# Revit family: 511_CA_HR-A_nailfin
name_source: partatom
category: Windows
revit_build: Autodesk Revit 2016 (Build: 20150220_1215(x64)
units: mm (PartAtom-declared; Revit-internal decimal feet)

## family parameters
Always vertical = Yes
Cut with Voids When Loaded = No
Host = Wall
OmniClass Number = 23.30.20.00
OmniClass Title = Windows
Room Calculation Point = No
Shared = No

## types (35) — shared parameters
Default Sill Height = 31 1/2"
MLW1 = 3 1/4"
MLW2 = 3 5/8"
MLW3 = 2 13/16"
Rough Height = 4 1/2"
Rough Width = 4 1/2"
Wall Closure = By host

## per-type parameters (varying)
| type | Bar Set | Height | MDLW | MLH | MLW4 | Width |
| 24x48 | 36" | 48" | 18" | 18" | 3" | 24" |
| 36x60 | 42" | 60" | 20" | 21" | 4 1/2" | 36" |
| 13.5x31.75Min | 19 3/4" | 31 3/4" | 20" | 9 7/8" | 1 11/16" | 13 1/2" |
| 36x120Max | 60" | 120" | 20" | 30" | 4 1/2" | 36" |
| 24x36 | 24" | 36" | 18" | 12" | 3" | 24" |
| 24x42 | 30" | 42" | 18" | 15" | 3" | 24" |
| 24x54 | 36" | 54" | 18" | 18" | 3" | 24" |
| 24x60 | 42" | 60" | 18" | 21" | 3" | 24" |
| 24x66 | 48" | 66" | 18" | 24" | 3" | 24" |
| 24x72 | 54" | 72" | 18" | 27" | 3" | 24" |
| 24x78 | 60" | 78" | 18" | 30" | 3" | 24" |
| 30x36 | 24" | 36" | 18" | 12" | 3 3/4" | 30" |
| 30x42 | 30" | 42" | 18" | 15" | 3 3/4" | 30" |
| 30x48 | 30" | 48" | 18" | 15" | 3 3/4" | 30" |
| 30x54 | 36" | 54" | 18" | 18" | 3 3/4" | 30" |
| 30x60 | 42" | 60" | 18" | 21" | 3 3/4" | 30" |
| 30x66 | 48" | 66" | 18" | 24" | 3 3/4" | 30" |
| 30x72 | 54" | 72" | 18" | 27" | 3 3/4" | 30" |
| 30x78 | 60" | 78" | 18" | 30" | 3 3/4" | 30" |
| 30x84 | 66" | 84" | 18" | 33" | 3 3/4" | 30" |
| 30x90 | 72" | 90" | 18" | 36" | 3 3/4" | 30" |
| 36x42 | 30" | 42" | 20" | 15" | 4 1/2" | 36" |
| 36x48 | 36" | 48" | 20" | 18" | 4 1/2" | 36" |
| 36x54 | 42" | 54" | 20" | 21" | 4 1/2" | 36" |
| 36x66 | 48" | 66" | 20" | 24" | 4 1/2" | 36" |
| 36x72 | 54" | 72" | 20" | 27" | 4 1/2" | 36" |
| 36x78 | 60" | 78" | 20" | 30" | 4 1/2" | 36" |
| 36x84 | 60" | 84" | 20" | 30" | 4 1/2" | 36" |
| 36x90 | 60" | 90" | 20" | 30" | 4 1/2" | 36" |
| 36x96 | 60" | 96" | 20" | 30" | 4 1/2" | 36" |
| 36x102 | 60" | 102" | 20" | 30" | 4 1/2" | 36" |
| 36x108 | 60" | 108" | 20" | 30" | 4 1/2" | 36" |
| 36x114 | 60" | 114" | 20" | 30" | 4 1/2" | 36" |
| 30x96 | 72" | 96" | 18" | 36" | 3 3/4" | 30" |
| 30x102 | 72" | 102" | 18" | 36" | 3 3/4" | 30" |

## geometry (parser evidence)
native form markers: Sweep x3
no freeform markers — native parametric forms only
